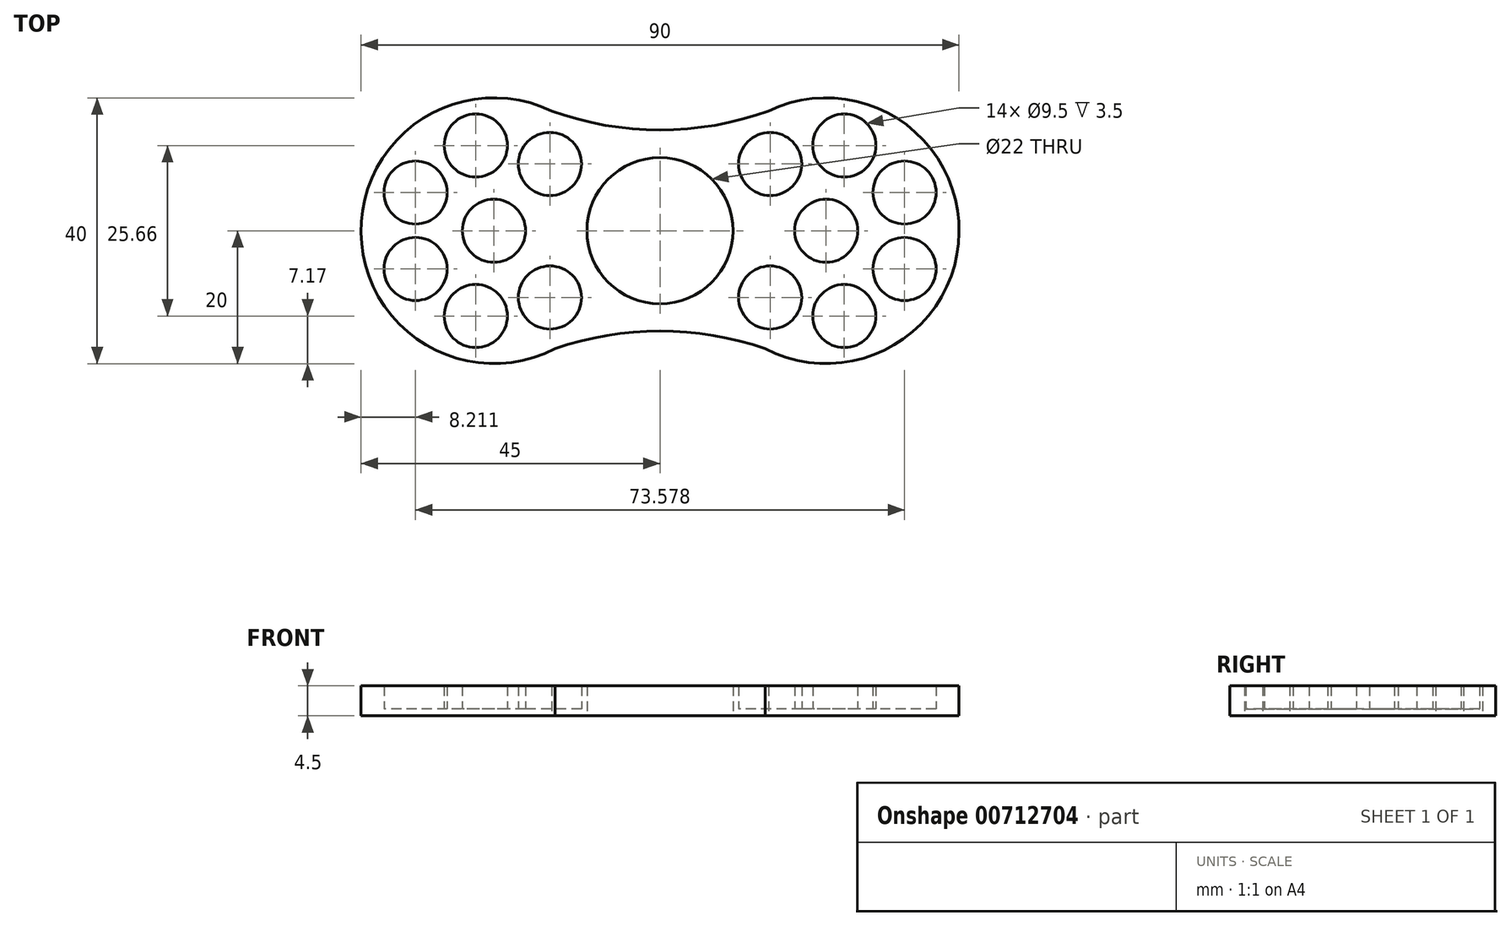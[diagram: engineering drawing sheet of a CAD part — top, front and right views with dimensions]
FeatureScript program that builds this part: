
annotation { "Feature Type Name" : "Feature", "Feature Type Description" : "" }
export const myFeature = defineFeature(function(context is Context, id is Id, definition is map)
    precondition{}
    {
        {
            var Q0;
            Q0=qCreatedBy(makeId("Top.planeOp"),FACE);
            var sketch = newSketch(context, id + "F0", { "sketchPlane" : qUnion([Q0])});
            skCircle(sketch, "E0", {"center": v(0, 0) * mm, "radius": 11 * mm});
            skPoint(sketch, "E1.center", {"position": v(-25, 0) * mm});
            skCircle(sketch, "E2", {"center": v(-25, 0) * mm, "radius": 4.75 * mm});
            skCircle(sketch, "E3", {"center": v(25, 0) * mm, "radius": 4.75 * mm});
            skArc(sketch, "E4.converted", {"start": v(15.82, -17.77) * mm, "mid": v(45, -0.28) * mm, "end": v(16.32, 18.02) * mm});
            skArc(sketch, "E5.converted", {"start": v(-16.32, 18.02) * mm, "mid": v(-45, -0.28) * mm, "end": v(-15.82, -17.77) * mm});
            skArc(sketch, "E6", {"start": v(-16.32, 18.02) * mm, "mid": v(0, 15.16) * mm, "end": v(16.32, 18.02) * mm});
            skArc(sketch, "E7", {"start": v(15.82, -17.77) * mm, "mid": v(0, -15.09) * mm, "end": v(-15.82, -17.77) * mm});
            skCircle(sketch, "E8", {"center": v(-16.57, 10.05) * mm, "radius": 4.75 * mm});
            skCircle(sketch, "E9.1.0", {"center": v(-27.73, 12.83) * mm, "radius": 4.75 * mm});
            skCircle(sketch, "E9.2.0", {"center": v(-36.79, 5.75) * mm, "radius": 4.75 * mm});
            skCircle(sketch, "E9.3.0", {"center": v(-36.79, -5.75) * mm, "radius": 4.75 * mm});
            skCircle(sketch, "E9.4.0", {"center": v(-27.73, -12.83) * mm, "radius": 4.75 * mm});
            skCircle(sketch, "E9.5.0", {"center": v(-16.57, -10.05) * mm, "radius": 4.75 * mm});
            skCircle(sketch, "E10", {"center": v(16.57, 10.05) * mm, "radius": 4.75 * mm});
            skCircle(sketch, "E11.1.0", {"center": v(27.73, 12.83) * mm, "radius": 4.75 * mm});
            skCircle(sketch, "E11.2.0", {"center": v(36.79, 5.75) * mm, "radius": 4.75 * mm});
            skCircle(sketch, "E11.3.0", {"center": v(36.79, -5.75) * mm, "radius": 4.75 * mm});
            skCircle(sketch, "E11.4.0", {"center": v(27.73, -12.83) * mm, "radius": 4.75 * mm});
            skCircle(sketch, "E11.5.0", {"center": v(16.57, -10.05) * mm, "radius": 4.75 * mm});
            skSolve(sketch);
        }
        {
            var Q0;
            Q0=makeQuery(id+"F0.imprint","IMPRINT",FACE,{"disambiguationData":[TD([[makeQuery(id+"F0.imprint","IMPRINT",EDGE,{"derivedFrom":sQuery(id+"F0.wireOp",EDGE,"E0")}),-1.0]])]});
            extrude(context, id + "F1", {"entities" : qUnion([Q0]), "depth" : 4.5 * mm, "offsetDistance" : 25 * mm});
        }
        {
            var Q0;
            Q0=makeQuery(id+"F0.imprint","IMPRINT",FACE,{"disambiguationData":[TD([[makeQuery(id+"F0.imprint","IMPRINT",EDGE,{"derivedFrom":sQuery(id+"F0.wireOp",EDGE,"4e1df6f6-e819-44f6-af3a-2e676c85ef9f.5.0")}),1.0]])]});
            var Q1;
            Q1=makeQuery(id+"F0.imprint","IMPRINT",FACE,{"disambiguationData":[TD([[makeQuery(id+"F0.imprint","IMPRINT",EDGE,{"derivedFrom":sQuery(id+"F0.wireOp",EDGE,"cZsZBCqV-I1pd-xoeP-Bse6-bLMjFn0RR5nI")}),1.0]])]});
            var Q2;
            Q2=makeQuery(id+"F0.imprint","IMPRINT",FACE,{"disambiguationData":[TD([[makeQuery(id+"F0.imprint","IMPRINT",EDGE,{"derivedFrom":sQuery(id+"F0.wireOp",EDGE,"4e1df6f6-e819-44f6-af3a-2e676c85ef9f.1.0")}),1.0]])]});
            var Q3;
            Q3=makeQuery(id+"F0.imprint","IMPRINT",FACE,{"disambiguationData":[TD([[makeQuery(id+"F0.imprint","IMPRINT",EDGE,{"derivedFrom":sQuery(id+"F0.wireOp",EDGE,"E2")}),1.0]])]});
            var Q4;
            Q4=makeQuery(id+"F0.imprint","IMPRINT",FACE,{"disambiguationData":[TD([[makeQuery(id+"F0.imprint","IMPRINT",EDGE,{"derivedFrom":sQuery(id+"F0.wireOp",EDGE,"4e1df6f6-e819-44f6-af3a-2e676c85ef9f.2.0")}),1.0]])]});
            var Q5;
            Q5=makeQuery(id+"F0.imprint","IMPRINT",FACE,{"disambiguationData":[TD([[makeQuery(id+"F0.imprint","IMPRINT",EDGE,{"derivedFrom":sQuery(id+"F0.wireOp",EDGE,"4e1df6f6-e819-44f6-af3a-2e676c85ef9f.3.0")}),1.0]])]});
            var Q6;
            Q6=makeQuery(id+"F0.imprint","IMPRINT",FACE,{"disambiguationData":[TD([[makeQuery(id+"F0.imprint","IMPRINT",EDGE,{"derivedFrom":sQuery(id+"F0.wireOp",EDGE,"4e1df6f6-e819-44f6-af3a-2e676c85ef9f.4.0")}),1.0]])]});
            var Q7;
            Q7=makeQuery(id+"F0.imprint","IMPRINT",FACE,{"disambiguationData":[TD([[makeQuery(id+"F0.imprint","IMPRINT",EDGE,{"derivedFrom":sQuery(id+"F0.wireOp",EDGE,"a3476362-ac5d-48c3-ac15-c6348dd78447.2.0")}),1.0]])]});
            var Q8;
            Q8=makeQuery(id+"F0.imprint","IMPRINT",FACE,{"disambiguationData":[TD([[makeQuery(id+"F0.imprint","IMPRINT",EDGE,{"derivedFrom":sQuery(id+"F0.wireOp",EDGE,"a3476362-ac5d-48c3-ac15-c6348dd78447.3.0")}),1.0]])]});
            var Q9;
            Q9=makeQuery(id+"F0.imprint","IMPRINT",FACE,{"disambiguationData":[TD([[makeQuery(id+"F0.imprint","IMPRINT",EDGE,{"derivedFrom":sQuery(id+"F0.wireOp",EDGE,"a3476362-ac5d-48c3-ac15-c6348dd78447.4.0")}),1.0]])]});
            var Q10;
            Q10=makeQuery(id+"F0.imprint","IMPRINT",FACE,{"disambiguationData":[TD([[makeQuery(id+"F0.imprint","IMPRINT",EDGE,{"derivedFrom":sQuery(id+"F0.wireOp",EDGE,"a3476362-ac5d-48c3-ac15-c6348dd78447.5.0")}),1.0]])]});
            var Q11;
            Q11=makeQuery(id+"F0.imprint","IMPRINT",FACE,{"disambiguationData":[TD([[makeQuery(id+"F0.imprint","IMPRINT",EDGE,{"derivedFrom":sQuery(id+"F0.wireOp",EDGE,"2CHyXEpP-o0Zd-GH8N-tCiF-7Rsv5rfd8QEF")}),1.0]])]});
            var Q12;
            Q12=makeQuery(id+"F0.imprint","IMPRINT",FACE,{"disambiguationData":[TD([[makeQuery(id+"F0.imprint","IMPRINT",EDGE,{"derivedFrom":sQuery(id+"F0.wireOp",EDGE,"a3476362-ac5d-48c3-ac15-c6348dd78447.1.0")}),1.0]])]});
            var Q13;
            Q13=makeQuery(id+"F0.imprint","IMPRINT",FACE,{"disambiguationData":[TD([[makeQuery(id+"F0.imprint","IMPRINT",EDGE,{"derivedFrom":sQuery(id+"F0.wireOp",EDGE,"4c46bda0-9f7e-4fa0-8a20-7f1ee8c03dad.4.0")}),1.0]])]});
            var Q14;
            Q14=makeQuery(id+"F0.imprint","IMPRINT",FACE,{"disambiguationData":[TD([[makeQuery(id+"F0.imprint","IMPRINT",EDGE,{"derivedFrom":sQuery(id+"F0.wireOp",EDGE,"4c46bda0-9f7e-4fa0-8a20-7f1ee8c03dad.5.0")}),1.0]])]});
            var Q15;
            Q15=makeQuery(id+"F0.imprint","IMPRINT",FACE,{"disambiguationData":[TD([[makeQuery(id+"F0.imprint","IMPRINT",EDGE,{"derivedFrom":sQuery(id+"F0.wireOp",EDGE,"4c46bda0-9f7e-4fa0-8a20-7f1ee8c03dad.3.0")}),1.0]])]});
            var Q16;
            Q16=makeQuery(id+"F0.imprint","IMPRINT",FACE,{"disambiguationData":[TD([[makeQuery(id+"F0.imprint","IMPRINT",EDGE,{"derivedFrom":sQuery(id+"F0.wireOp",EDGE,"4c46bda0-9f7e-4fa0-8a20-7f1ee8c03dad.2.0")}),1.0]])]});
            var Q17;
            Q17=makeQuery(id+"F0.imprint","IMPRINT",FACE,{"disambiguationData":[TD([[makeQuery(id+"F0.imprint","IMPRINT",EDGE,{"derivedFrom":sQuery(id+"F0.wireOp",EDGE,"4c46bda0-9f7e-4fa0-8a20-7f1ee8c03dad.1.0")}),1.0]])]});
            var Q18;
            Q18=makeQuery(id+"F0.imprint","IMPRINT",FACE,{"disambiguationData":[TD([[makeQuery(id+"F0.imprint","IMPRINT",EDGE,{"derivedFrom":sQuery(id+"F0.wireOp",EDGE,"XCqX1WRV-f8Rd-YJQW-DoSE-vuXeSPOKY4FF")}),1.0]])]});
            var Q19;
            Q19=makeQuery(id+"F0.imprint","IMPRINT",FACE,{"disambiguationData":[TD([[makeQuery(id+"F0.imprint","IMPRINT",EDGE,{"derivedFrom":sQuery(id+"F0.wireOp",EDGE,"44d366ba-ee16-499c-b8f7-130e9abb6c3f.5.0")}),1.0]])]});
            var Q20;
            Q20=makeQuery(id+"F0.imprint","IMPRINT",FACE,{"disambiguationData":[TD([[makeQuery(id+"F0.imprint","IMPRINT",EDGE,{"derivedFrom":sQuery(id+"F0.wireOp",EDGE,"44d366ba-ee16-499c-b8f7-130e9abb6c3f.4.0")}),1.0]])]});
            var Q21;
            Q21=makeQuery(id+"F0.imprint","IMPRINT",FACE,{"disambiguationData":[TD([[makeQuery(id+"F0.imprint","IMPRINT",EDGE,{"derivedFrom":sQuery(id+"F0.wireOp",EDGE,"44d366ba-ee16-499c-b8f7-130e9abb6c3f.3.0")}),1.0]])]});
            var Q22;
            Q22=makeQuery(id+"F0.imprint","IMPRINT",FACE,{"disambiguationData":[TD([[makeQuery(id+"F0.imprint","IMPRINT",EDGE,{"derivedFrom":sQuery(id+"F0.wireOp",EDGE,"44d366ba-ee16-499c-b8f7-130e9abb6c3f.2.0")}),1.0]])]});
            var Q23;
            Q23=makeQuery(id+"F0.imprint","IMPRINT",FACE,{"disambiguationData":[TD([[makeQuery(id+"F0.imprint","IMPRINT",EDGE,{"derivedFrom":sQuery(id+"F0.wireOp",EDGE,"44d366ba-ee16-499c-b8f7-130e9abb6c3f.1.0")}),1.0]])]});
            var Q24;
            Q24=makeQuery(id+"F0.imprint","IMPRINT",FACE,{"disambiguationData":[TD([[makeQuery(id+"F0.imprint","IMPRINT",EDGE,{"derivedFrom":sQuery(id+"F0.wireOp",EDGE,"k0PYirwU-Hx2L-nOe0-gXHO-UjKAI2IcQulI")}),1.0]])]});
            var Q25;
            Q25=makeQuery(id+"F0.imprint","IMPRINT",FACE,{"disambiguationData":[TD([[makeQuery(id+"F0.imprint","IMPRINT",EDGE,{"derivedFrom":sQuery(id+"F0.wireOp",EDGE,"E3")}),1.0]])]});
            var Q26;
            Q26=makeQuery(id+"F0.imprint","IMPRINT",FACE,{"disambiguationData":[TD([[makeQuery(id+"F0.imprint","IMPRINT",EDGE,{"derivedFrom":sQuery(id+"F0.wireOp",EDGE,"E8")}),1.0]])]});
            var Q27;
            Q27=makeQuery(id+"F0.imprint","IMPRINT",FACE,{"disambiguationData":[TD([[makeQuery(id+"F0.imprint","IMPRINT",EDGE,{"derivedFrom":sQuery(id+"F0.wireOp",EDGE,"E9.1.0")}),1.0]])]});
            var Q28;
            Q28=makeQuery(id+"F0.imprint","IMPRINT",FACE,{"disambiguationData":[TD([[makeQuery(id+"F0.imprint","IMPRINT",EDGE,{"derivedFrom":sQuery(id+"F0.wireOp",EDGE,"E9.2.0")}),1.0]])]});
            var Q29;
            Q29=makeQuery(id+"F0.imprint","IMPRINT",FACE,{"disambiguationData":[TD([[makeQuery(id+"F0.imprint","IMPRINT",EDGE,{"derivedFrom":sQuery(id+"F0.wireOp",EDGE,"E9.3.0")}),1.0]])]});
            var Q30;
            Q30=makeQuery(id+"F0.imprint","IMPRINT",FACE,{"disambiguationData":[TD([[makeQuery(id+"F0.imprint","IMPRINT",EDGE,{"derivedFrom":sQuery(id+"F0.wireOp",EDGE,"E9.4.0")}),1.0]])]});
            var Q31;
            Q31=makeQuery(id+"F0.imprint","IMPRINT",FACE,{"disambiguationData":[TD([[makeQuery(id+"F0.imprint","IMPRINT",EDGE,{"derivedFrom":sQuery(id+"F0.wireOp",EDGE,"E9.5.0")}),1.0]])]});
            var Q32;
            Q32=makeQuery(id+"F0.imprint","IMPRINT",FACE,{"disambiguationData":[TD([[makeQuery(id+"F0.imprint","IMPRINT",EDGE,{"derivedFrom":sQuery(id+"F0.wireOp",EDGE,"E10")}),1.0]])]});
            var Q33;
            Q33=makeQuery(id+"F0.imprint","IMPRINT",FACE,{"disambiguationData":[TD([[makeQuery(id+"F0.imprint","IMPRINT",EDGE,{"derivedFrom":sQuery(id+"F0.wireOp",EDGE,"E11.1.0")}),1.0]])]});
            var Q34;
            Q34=makeQuery(id+"F0.imprint","IMPRINT",FACE,{"disambiguationData":[TD([[makeQuery(id+"F0.imprint","IMPRINT",EDGE,{"derivedFrom":sQuery(id+"F0.wireOp",EDGE,"E11.2.0")}),1.0]])]});
            var Q35;
            Q35=makeQuery(id+"F0.imprint","IMPRINT",FACE,{"disambiguationData":[TD([[makeQuery(id+"F0.imprint","IMPRINT",EDGE,{"derivedFrom":sQuery(id+"F0.wireOp",EDGE,"E11.3.0")}),1.0]])]});
            var Q36;
            Q36=makeQuery(id+"F0.imprint","IMPRINT",FACE,{"disambiguationData":[TD([[makeQuery(id+"F0.imprint","IMPRINT",EDGE,{"derivedFrom":sQuery(id+"F0.wireOp",EDGE,"E11.4.0")}),1.0]])]});
            var Q37;
            Q37=makeQuery(id+"F0.imprint","IMPRINT",FACE,{"disambiguationData":[TD([[makeQuery(id+"F0.imprint","IMPRINT",EDGE,{"derivedFrom":sQuery(id+"F0.wireOp",EDGE,"E11.5.0")}),1.0]])]});
            extrude(context, id + "F2", {"entities" : qUnion([Q0, Q1, Q2, Q3, Q4, Q5, Q6, Q7, Q8, Q9, Q10, Q11, Q12, Q13, Q14, Q15, Q16, Q17, Q18, Q19, Q20, Q21, Q22, Q23, Q24, Q25, Q26, Q27, Q28, Q29, Q30, Q31, Q32, Q33, Q34, Q35, Q36, Q37]), "operationType" : NewBodyOperationType.ADD, "depth" : 1 * mm, "offsetDistance" : 25 * mm});
        }
    });
